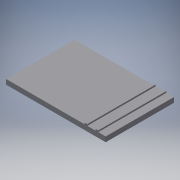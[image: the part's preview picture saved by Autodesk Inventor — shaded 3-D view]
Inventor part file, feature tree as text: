
AUTODESK INVENTOR PART (.ipt)
format: ipt  version: 2018.3 (Build 223284000, 284)  size: 110,080 bytes
history: native  units: mm
features: extrude x2, sketch x2
ambient origin geometry x8: Origin, YZ Plane, XZ Plane, XY Plane, X Axis, Y Axis, Z Axis, Center Point
bodies: Solid1 (feature_tree)
feature tree (4):
  extrude  "Extrusion1"  Depth=13.7mm
  extrude  "Extrusion2"  Depth=1.0mm
  sketch  "Sketch1"  dims[d0=20.0mm d1=13.7mm]
  sketch  "Sketch2"  dims[d2=1.0mm d3=0.0mm d4=1.0mm d5=1.0mm d6=1.8mm d7=0.8mm d8=0.0mm d9=3.5mm]
